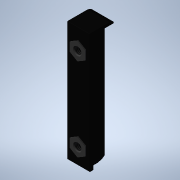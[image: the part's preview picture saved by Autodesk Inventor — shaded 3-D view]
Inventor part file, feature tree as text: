
AUTODESK INVENTOR PART (.ipt)
format: ipt  version: 2024.3 (Build 283343000, 343)  size: 257,536 bytes
history: native  units: mm
features: other x35, sketch x7, extrude x5, revolve x2, thread x2
ambient origin geometry x8: Origin, YZ Plane, XZ Plane, XY Plane, X Axis, Y Axis, Z Axis, Center Point
bodies: Solid1 (feature_tree)
feature tree (51):
  extrude  "Extrusion1"  Depth=42.8mm TaperAngle=0.0deg
  extrude  "Extrusion2"  Depth=0.4mm TaperAngle=0.0deg
  extrude  "Extrusion3"  TaperAngle=360.0deg  [1 undecoded]
  sketch  "Sketch_11"  dims[d14=1.259mm d15=0.0mm d16=0.0mm]
  extrude  "Extrusion4"  TaperAngle=360.0deg  [1 undecoded]
  extrude  "Extrusion5"  TaperAngle=0.0deg  [1 undecoded]
  revolve  "Revolution1"  [1 undecoded]
  thread  "Thread1"  [1 undecoded]
  revolve  "Revolution2"  [1 undecoded]
  thread  "Thread2"  [1 undecoded]
  other  "ANBAU_XY"
  other  "ANBAU_YZ"
  other  "ANBAU_ZX"
  other  "ANBAU_X"
  other  "ANBAU_Y"
  other  "ANBAU_Z"
  other  "ANBAU_Center"
  other  "ANBAU_2_XY"
  other  "ANBAU_2_YZ"
  other  "ANBAU_2_ZX"
  other  "ANBAU_2_X"
  other  "ANBAU_2_Y"
  other  "ANBAU_2_Z"
  other  "ANBAU_2_Center"
  other  "IP1_XY"
  other  "IP1_YZ"
  other  "IP1_ZX"
  other  "IP1_X"
  other  "IP1_Y"
  other  "IP1_Z"
  other  "IP1_Center"
  other  "IP_ANBAU_XY"
  other  "IP_ANBAU_YZ"
  other  "IP_ANBAU_ZX"
  other  "IP_ANBAU_X"
  other  "IP_ANBAU_Y"
  other  "IP_ANBAU_Z"
  other  "IP_ANBAU_Center"
  other  "IP_ANBAU_2_XY"
  other  "IP_ANBAU_2_YZ"
  other  "IP_ANBAU_2_ZX"
  other  "IP_ANBAU_2_X"
  other  "IP_ANBAU_2_Y"
  other  "IP_ANBAU_2_Z"
  other  "IP_ANBAU_2_Center"
  sketch  "Sketch_1"  dims[d0=8.0mm d1=0.0mm d2=42.8mm d3=0.0mm]
  sketch  "Sketch_6"  dims[d4=4.0mm d5=0.0mm d6=0.4mm d7=0.0mm]
  sketch  "Sketch_9"  dims[d8=0.4mm d9=0.0mm d10=360.0deg]
  sketch  "Sketch_12"
  sketch  "Sketch_10"  dims[d11=1.259mm d12=0.0mm d13=360.0deg]
  sketch  "Sketch_13"
note: 7 required parameter values undecoded (feature->parameter linkage not recoverable at this tier; creation-order binding heuristic only, values carry confidence <= 0.55)
